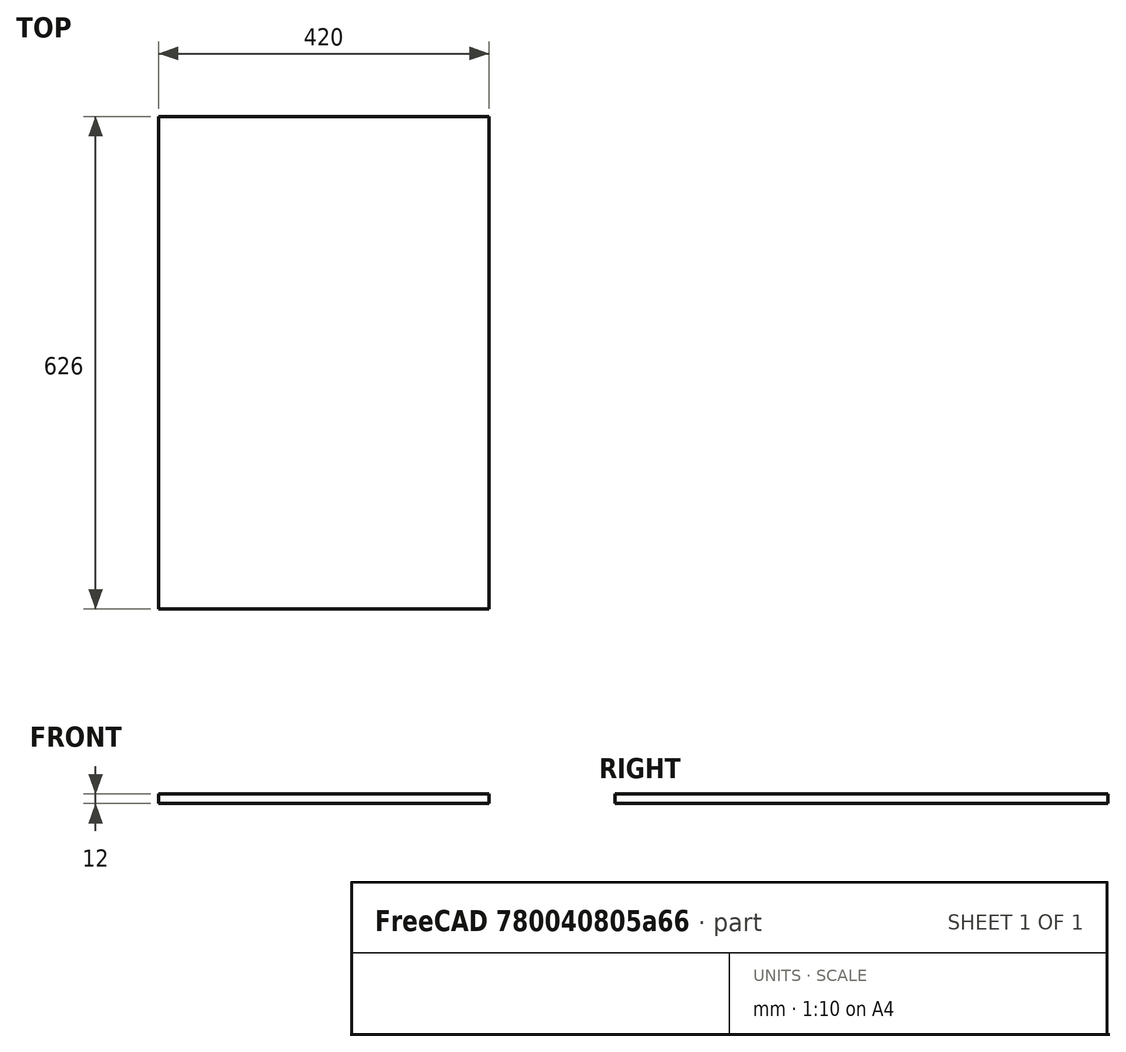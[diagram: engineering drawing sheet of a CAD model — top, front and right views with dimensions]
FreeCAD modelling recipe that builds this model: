
FCSTD DOCUMENT  (FreeCAD 0.18R16131 (Git))
Label: bottom_plate
License: All rights reserved
LicenseURL: http://en.wikipedia.org/wiki/All_rights_reserved
objects: Sketcher::SketchObject×1, PartDesign::Pad×1, PartDesign::Body×1
note: 4 computed .brp shape members not serialized (recipe doc carries the construction recipe); baked Part::Feature solids carry a one-line shape summary decoded from their .brp

FEATURE [Sketcher::SketchObject] Sketch
  MapMode = 5
  Support = -> [XY_Plane]
  sketch-geometry (4):
    g0: LineSegment StartX=0 StartY=0 StartZ=0 EndX=420 EndY=0 EndZ=0
    g1: LineSegment StartX=420 StartY=0 StartZ=0 EndX=420 EndY=626 EndZ=0
    g2: LineSegment StartX=420 StartY=626 StartZ=0 EndX=0 EndY=626 EndZ=0
    g3: LineSegment StartX=0 StartY=626 StartZ=0 EndX=0 EndY=0 EndZ=0
  constraints (11):
    c: Coincident(g0,g1)
    c: Coincident(g1,g2)
    c: Coincident(g2,g3)
    c: Coincident(g3,g0)
    c: Horizontal(g0)
    c: Horizontal(g2)
    c: Vertical(g1)
    c: Vertical(g3)
    c: Coincident(g0,g-1)
    c: DistanceX(g2,g2) = 420
    c: DistanceY(g3,g3) = 626
FEATURE [PartDesign::Pad] Pad
  Length = 12
  Length2 = 100
  Profile = -> Sketch
  Type = 0
FEATURE [PartDesign::Body] Body
  Group = -> [Sketch,Pad]
  Origin = -> Origin
  Tip = -> Pad
